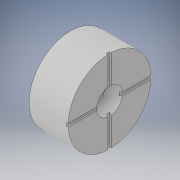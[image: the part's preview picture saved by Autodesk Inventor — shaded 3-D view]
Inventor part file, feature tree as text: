
AUTODESK INVENTOR PART (.ipt)
format: ipt  version: 2019 (Build 230136000, 136)  size: 165,376 bytes
history: native  units: mm
features: sketch x2, revolve x1, extrude x1, other x1
ambient origin geometry x8: Origin, YZ Plane, XZ Plane, XY Plane, X Axis, Y Axis, Z Axis, Center Point
bodies: Solid1 (feature_tree)
feature tree (5):
  revolve  "Revolution1"  [1 undecoded]
  extrude  "Extrusion2"  Depth=0.5mm
  sketch  "Sketch2"  dims[d10=0.0mm d11=10.0mm d12=34.906585mm]
  other  "2D Equation Curve2"
  sketch  "Sketch4"  dims[d13=5.0mm d18=6.35mm d19=2.0mm d34=0.5mm d35=0.25mm d36=12.7mm d37=12.7mm d38=0.5mm d39=0.25mm d40=12.7mm d41=12.7mm d42=0.25mm d43=0.0mm]
note: 1 required parameter value undecoded (feature->parameter linkage not recoverable at this tier; creation-order binding heuristic only, values carry confidence <= 0.55)
